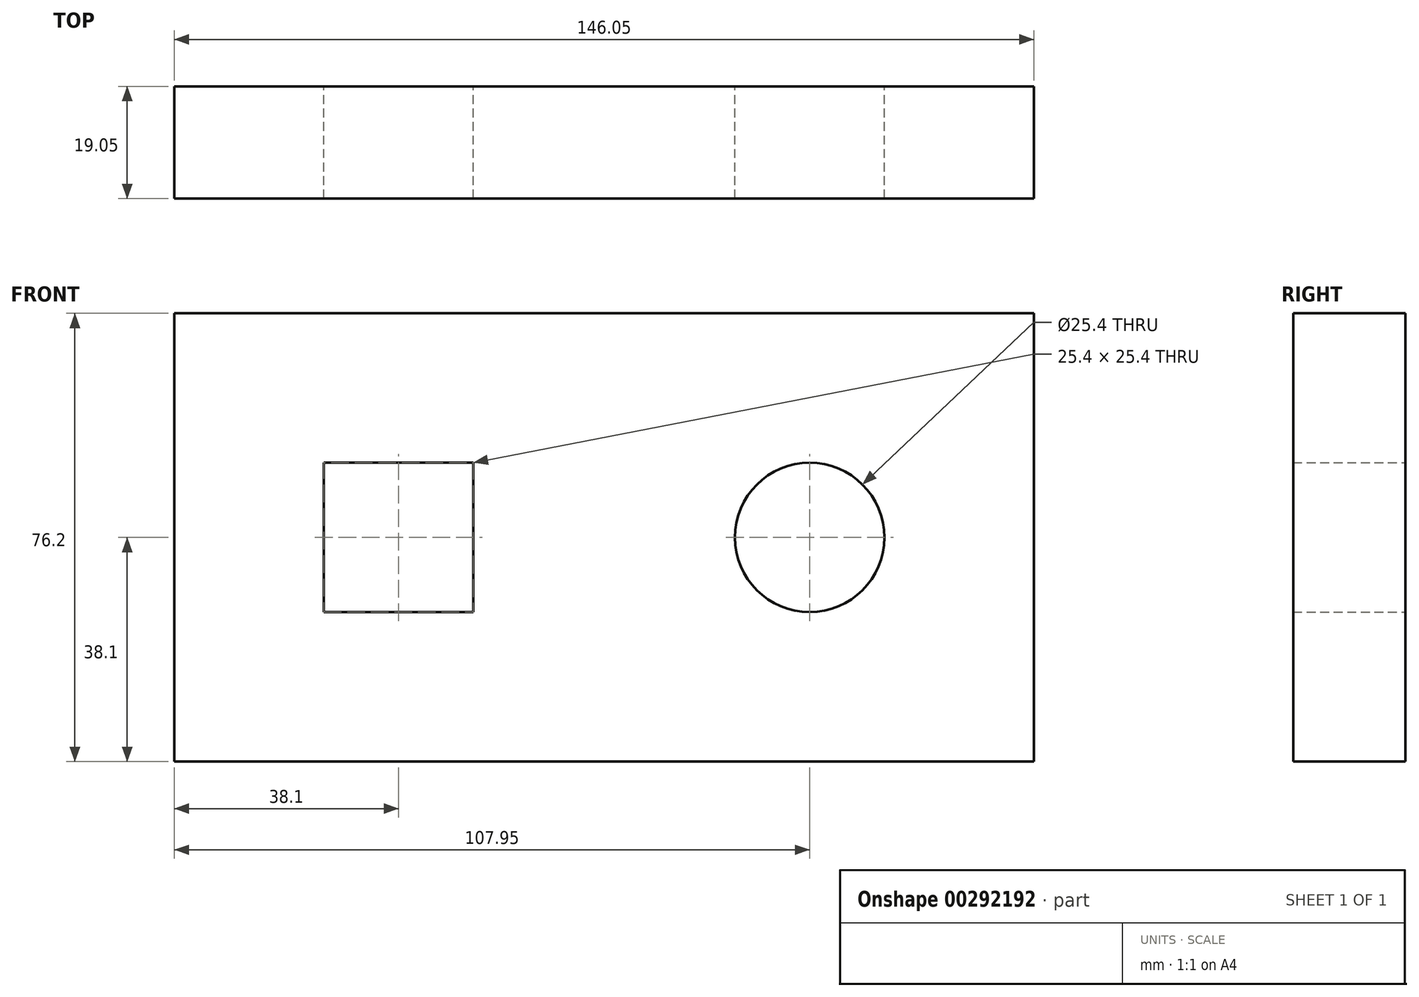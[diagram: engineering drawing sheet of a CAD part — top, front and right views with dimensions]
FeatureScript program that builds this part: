
annotation { "Feature Type Name" : "Feature", "Feature Type Description" : "" }
export const myFeature = defineFeature(function(context is Context, id is Id, definition is map)
    precondition{}
    {
        {
            var Q0;
            Q0=qCreatedBy(makeId("Front.planeOp"),FACE);
            var sketch = newSketch(context, id + "F0", { "sketchPlane" : qUnion([Q0])});
            skLineSegment(sketch, "E0.bottom", {"start": v(0, 0) * mm, "end": v(-146.05, 0) * mm});
            skLineSegment(sketch, "E0.top", {"start": v(0, 76.2) * mm, "end": v(-146.05, 76.2) * mm});
            skLineSegment(sketch, "E0.left", {"start": v(0, 0) * mm, "end": v(0, 76.2) * mm});
            skLineSegment(sketch, "E0.right", {"start": v(-146.05, 0) * mm, "end": v(-146.05, 76.2) * mm});
            skCircle(sketch, "E1", {"center": v(-38.1, 38.1) * mm, "radius": 12.7 * mm});
            skLineSegment(sketch, "E2.bottom", {"start": v(-120.65, 50.8) * mm, "end": v(-95.25, 50.8) * mm});
            skLineSegment(sketch, "E2.top", {"start": v(-120.65, 25.4) * mm, "end": v(-95.25, 25.4) * mm});
            skLineSegment(sketch, "E2.left", {"start": v(-120.65, 50.8) * mm, "end": v(-120.65, 25.4) * mm});
            skLineSegment(sketch, "E2.right", {"start": v(-95.25, 50.8) * mm, "end": v(-95.25, 25.4) * mm});
            skSolve(sketch);
        }
        {
            var Q0;
            Q0 = qSketchRegion(id + "F0", true);
            extrude(context, id + "F1", {"entities" : qUnion([Q0]), "depth" : 19.05 * mm});
        }
    });
